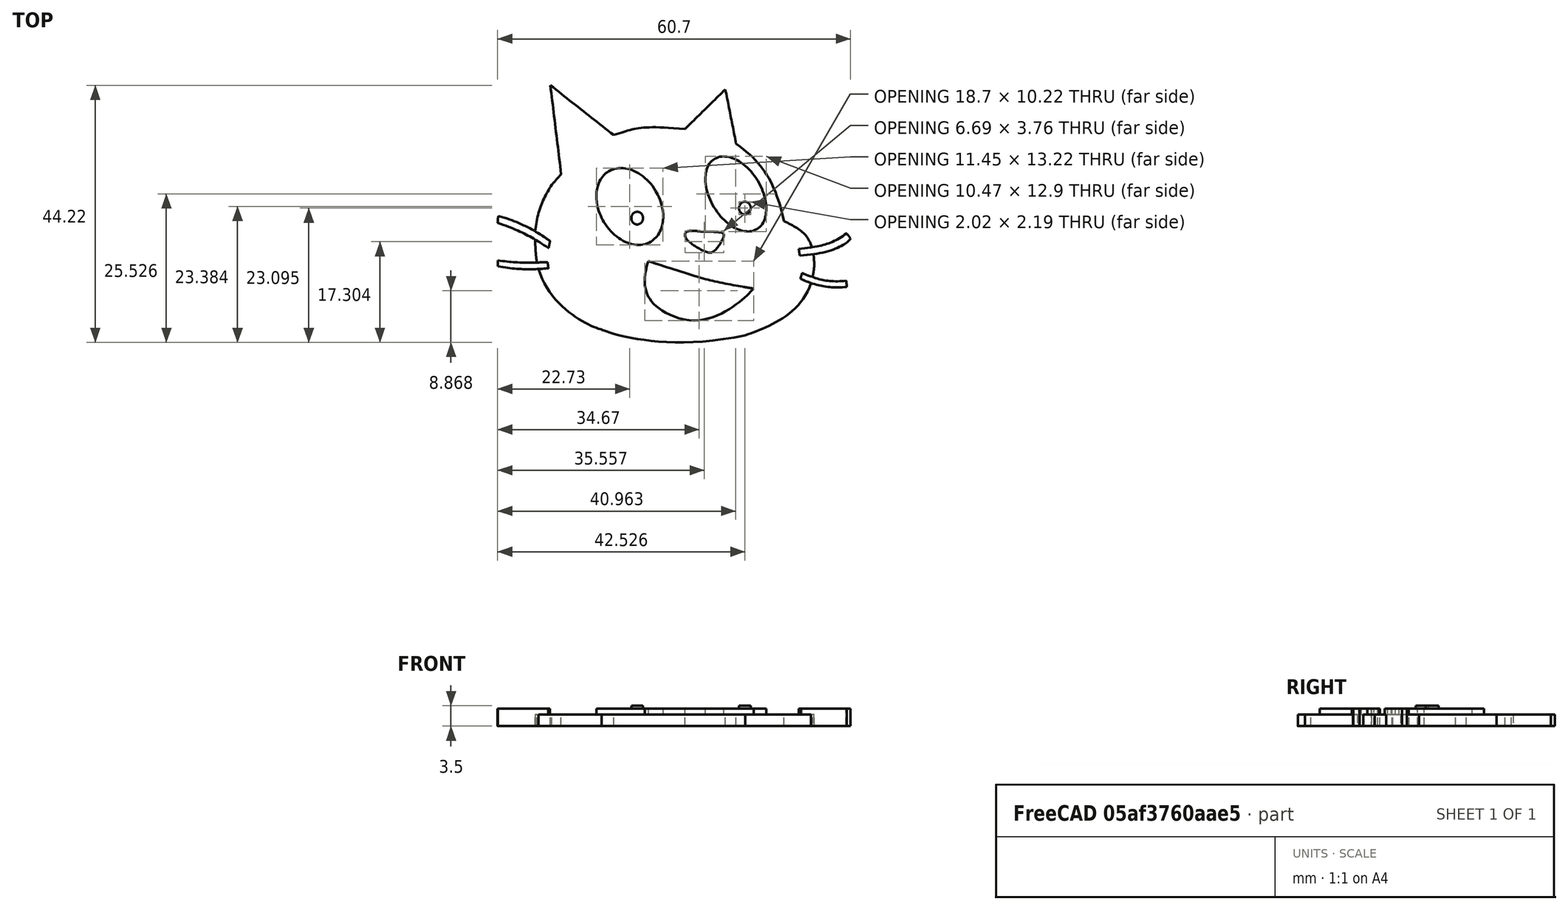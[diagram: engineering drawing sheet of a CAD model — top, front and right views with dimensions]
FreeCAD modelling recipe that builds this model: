
FCSTD DOCUMENT  (FreeCAD 0.14R3702 (Git))
Label: scratch_face
License: CC-BY 3.0
LicenseURL: http://creativecommons.org/licenses/by/3.0/
objects: Part::Feature×11, Part::Extrusion×11, Part::MultiFuse×1
note: 23 computed .brp shape members not serialized (recipe doc carries the construction recipe); baked Part::Feature solids carry a one-line shape summary decoded from their .brp

FEATURE [Part::Feature] path3150
  shape: bbox 48.25 x 45.35 x 2e-07 mm, 0 faces, 0 solids (baked)
FEATURE [Part::Feature] path3973_2
  shape: bbox 12.16 x 13.86 x 2e-07 mm, 0 faces, 0 solids (baked)
FEATURE [Part::Feature] path3981_6
  shape: bbox 11.18 x 13.57 x 2e-07 mm, 0 faces, 0 solids (baked)
FEATURE [Part::Feature] path3989_6
  shape: bbox 2.026 x 2.2 x 2e-07 mm, 1 faces, 0 solids (baked)
FEATURE [Part::Feature] path3985_7
  shape: bbox 2.02 x 2.197 x 2e-07 mm, 1 faces, 0 solids (baked)
FEATURE [Part::Feature] path4045_0
  shape: bbox 19.5 x 11.04 x 2e-07 mm, 0 faces, 0 solids (baked)
FEATURE [Part::Feature] path3993_1_6
  shape: bbox 6.742 x 3.801 x 2e-07 mm, 1 faces, 0 solids (baked)
FEATURE [Part::Feature] path2994
  shape: bbox 9.018 x 5.518 x 2e-07 mm, 0 faces, 0 solids (baked)
FEATURE [Part::Feature] path2996
  shape: bbox 8.682 x 1.641 x 2e-07 mm, 0 faces, 0 solids (baked)
FEATURE [Part::Feature] path2998
  shape: bbox 8.914 x 3.82 x 2e-07 mm, 0 faces, 0 solids (baked)
FEATURE [Part::Feature] path3000
  shape: bbox 7.988 x 2.613 x 2e-07 mm, 0 faces, 0 solids (baked)
FEATURE [Part::Extrusion] Extrude
  Base = -> path3150
  Dir = (0,0,2)
  Solid = true
FEATURE [Part::Extrusion] Extrude001
  Base = -> path3973_2
  Dir = (0,0,3)
  Solid = true
FEATURE [Part::Extrusion] Extrude002
  Base = -> path3981_6
  Dir = (0,0,3)
  Solid = true
FEATURE [Part::Extrusion] Extrude003
  Base = -> path3989_6
  Dir = (0,0,3.5)
  Solid = true
FEATURE [Part::Extrusion] Extrude004
  Base = -> path3985_7
  Dir = (0,0,3.5)
  Solid = true
FEATURE [Part::Extrusion] Extrude005
  Base = -> path4045_0
  Dir = (0,0,3)
  Solid = true
FEATURE [Part::Extrusion] Extrude006
  Base = -> path3993_1_6
  Dir = (0,0,3)
  Solid = true
FEATURE [Part::Extrusion] Extrude007
  Base = -> path2994
  Dir = (0,0,3)
  Solid = true
FEATURE [Part::Extrusion] Extrude008
  Base = -> path2996
  Dir = (0,0,3)
  Solid = true
FEATURE [Part::Extrusion] Extrude009
  Base = -> path2998
  Dir = (0,0,3)
  Solid = true
FEATURE [Part::Extrusion] Extrude010
  Base = -> path3000
  Dir = (0,0,3)
  Solid = true
FEATURE [Part::MultiFuse] Fusion
  Shapes = -> [Extrude,Extrude005,Extrude004,Extrude006,Extrude001,Extrude002,Extrude007,Extrude008,Extrude010,Extrude009,Extrude003]
